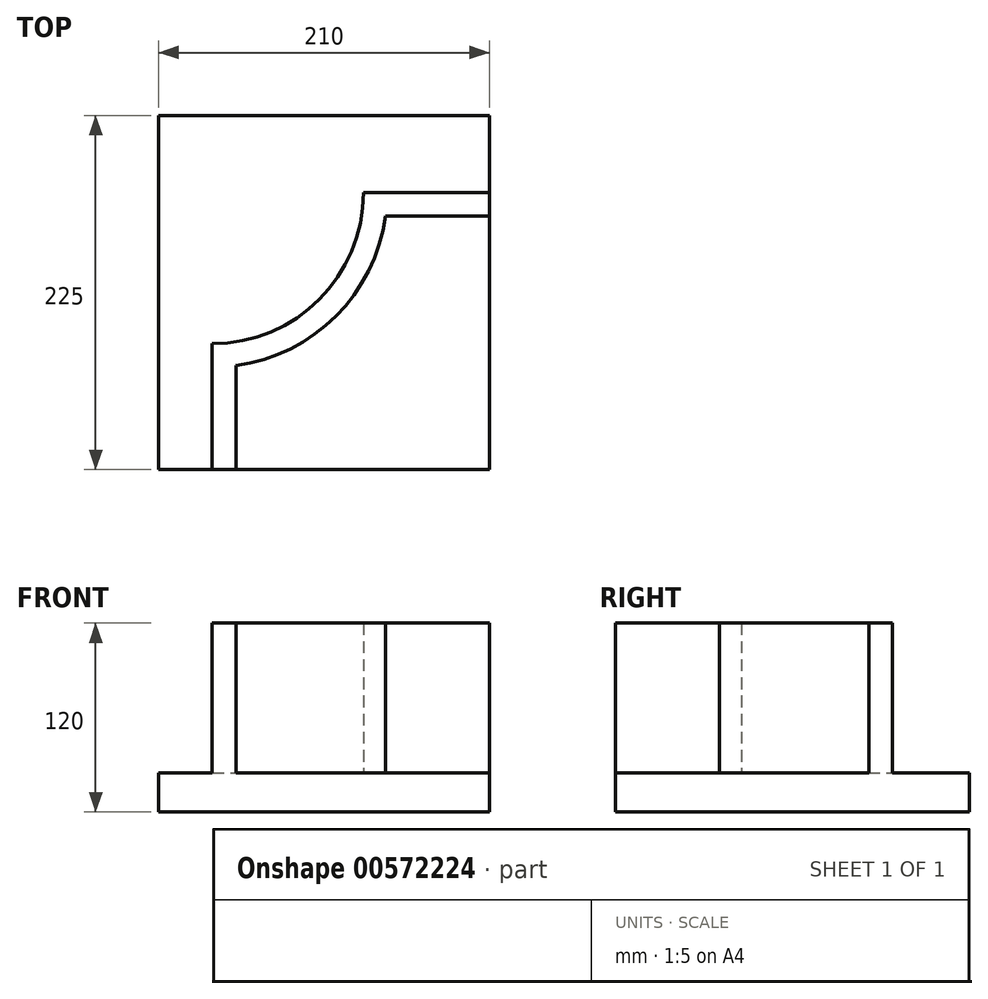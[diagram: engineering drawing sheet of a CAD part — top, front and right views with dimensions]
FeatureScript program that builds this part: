
annotation { "Feature Type Name" : "Feature", "Feature Type Description" : "" }
export const myFeature = defineFeature(function(context is Context, id is Id, definition is map)
    precondition{}
    {
        {
            var Q0;
            Q0=qCreatedBy(makeId("Top.planeOp"),FACE);
            var sketch = newSketch(context, id + "F0", { "sketchPlane" : qUnion([Q0])});
            skLineSegment(sketch, "E0.bottom", {"start": v(105, -112.5) * mm, "end": v(-105, -112.5) * mm});
            skLineSegment(sketch, "E0.top", {"start": v(105, 112.5) * mm, "end": v(-105, 112.5) * mm});
            skLineSegment(sketch, "E0.left", {"start": v(105, -112.5) * mm, "end": v(105, 112.5) * mm});
            skLineSegment(sketch, "E0.right", {"start": v(-105, -112.5) * mm, "end": v(-105, 112.5) * mm});
            skPoint(sketch, "E0.middle", {"position": v(0, 0) * mm});
            skSolve(sketch);
        }
        {
            var Q0;
            Q0=makeQuery(id+"F0.imprint","IMPRINT",FACE,{"disambiguationData":[TD([[makeQuery(id+"F0.imprint","IMPRINT",EDGE,{"derivedFrom":sQuery(id+"F0.wireOp",EDGE,"E0.bottom")}),-1.0]])]});
            extrude(context, id + "F1", {"entities" : qUnion([Q0]), "depth" : 25 * mm, "offsetDistance" : 25 * mm});
        }
        {
            var Q0;
            Q0=makeQuery(id+"F1.opExtrude","CAP_FACE",FACE,{"disambiguationData":[OSD([sQuery(id+"F0.wireOp",EDGE,"E0.bottom"),sQuery(id+"F0.wireOp",EDGE,"E0.top"),sQuery(id+"F0.wireOp",EDGE,"E0.left"),sQuery(id+"F0.wireOp",EDGE,"E0.right")])],"isStart":false});
            var sketch = newSketch(context, id + "F2", { "sketchPlane" : qUnion([Q0])});
            skLineSegment(sketch, "E1", {"start": v(-71, -112.5) * mm, "end": v(-71, -32.5) * mm});
            skLineSegment(sketch, "E2", {"start": v(105, 63.5) * mm, "end": v(25, 63.5) * mm});
            skArc(sketch, "E3", {"start": v(-71, -32.5) * mm, "mid": v(-3.12, -4.38) * mm, "end": v(25, 63.5) * mm});
            skLineSegment(sketch, "E4", {"start": v(-71, 63.5) * mm, "end": v(25, 63.5) * mm, "construction": true});
            skLineSegment(sketch, "E5", {"start": v(-71, 63.5) * mm, "end": v(-71, -32.5) * mm, "construction": true});
            skLineSegment(sketch, "E6.0", {"start": v(-56, -112.5) * mm, "end": v(-56, -46.48) * mm});
            skArc(sketch, "E6.1", {"start": v(-56, -46.48) * mm, "mid": v(7.49, -14.99) * mm, "end": v(38.98, 48.5) * mm});
            skLineSegment(sketch, "E6.2", {"start": v(105, 48.5) * mm, "end": v(38.98, 48.5) * mm});
            skLineSegment(sketch, "E7.0", {"start": v(105, -112.5) * mm, "end": v(105, 112.5) * mm});
            skLineSegment(sketch, "E8.0", {"start": v(105, -112.5) * mm, "end": v(-105, -112.5) * mm});
            skSolve(sketch);
        }
        {
            var Q0;
            {var subQ2=sQuery(id+"F2.wireOp",EDGE,"E1");Q0=makeQuery(id+"F2.imprint","IMPRINT",FACE,{"disambiguationData":[TD([[makeQuery(id+"F2.imprint","IMPRINT",EDGE,{"derivedFrom":subQ2}),-1.0]])]});}
            extrude(context, id + "F3", {"entities" : qUnion([Q0]), "operationType" : NewBodyOperationType.ADD, "depth" : 95 * mm, "offsetDistance" : 25 * mm});
        }
    });
